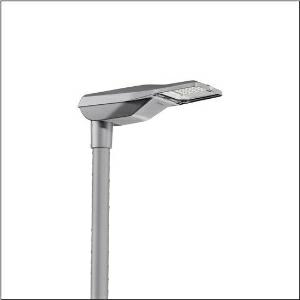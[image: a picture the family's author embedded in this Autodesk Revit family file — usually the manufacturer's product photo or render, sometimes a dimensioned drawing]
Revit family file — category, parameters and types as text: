
# Revit family: streetlight_sl_21_iq_micro___st0_8a_5xe1c31d08cb_88cc
name_source: partatom
category: Lighting Fixtures
units: mm (PartAtom-declared; Revit-internal decimal feet)

## family parameters
Cut with Voids When Loaded = No
Host = Face
Light Source = No
Part Type = Normal
Room Calculation Point = No
Round Connector Dimension = Use Diameter
Shared = No

## types (1)
- --- (1 x LED, 2870 lm, 19.4 W, 3000K)
    Apparent Load = 19 VA
    CIE Flux Codes = 38 75 97 100 100
    Color Rendering = 70
    Color Temperature = 3000K
    Default Elevation = 1800 mm
    Description = Streetlight SL 21 iQ micro, mast luminaire, primary light control with lens, of PMMA, primary optical cover: cover, of toughened safety glass, transparent, light distribution: ST0.8a, light emission: direct distribution, primary light characteristic: asymmetric, installation type: post-top, side-entry, LED, High Power LED, rated luminous flux: 2.870lm, luminous efficacy: 148lm/W, light colour: 730, colour temperature: 3000K, control gear: iQ-Comfort, control: Auto-Match, Temp-Guard, Lumen-Switch, Night-Set, Smart-Wire, Light-Fading, Desk-Remote (wireless, voltage-free reading and setting of iQ features in the workshop via application-optimized NFC function/RFID function), optimised constant luminous flux control (CLO 2.0), pre-setting: linear dimming characteristic, mains connection: 220..240V, AC, 50/60Hz, start of lifetime: 19W, end of service life: 20W, reduction: 10W, luminaire housing, of diecast aluminium, powder-coated, Siteco® metallic grey (DB 702S), corrosivity category C5 mid according to DIN EN ISO 12944, please order mast flange separately, inclination adjustable: 0°, 5°, 10°, 15°, sealing non-destructively replaceable, multi-level sealing system, length: 528mm, width: 235mm, height: 110mm, mast flange for spigot size: 42mm (side-entry): 5XC10008XM4, 60/48mm (side-entry/post-top): 5XC10108XM2, 76/60mm (side-entry/post-top): 5XC10108XM1, protection rating (complete): IP66, insulation class (complete): insulation class II (safety insulation), certification: CE, ENEC, ENEC+, VDE, impact resistance: IK10, permissible operating ambient temperature for outdoor applications: -40..+50°C, standard-compliant lighting for roads and squares, packaging unit: 1 piece

Light Distribution: ST0.8a
    Height = 110 mm
    Lamp = 1 x LED
    Lamp Light Flux = 2870 lm
    Lamp Power = 19.4 W
    Lamp count = 1
    Length = 528 mm
    Luminous efficacy = 148 lm/W
    Manufacturer = Siteco
    ModVariant = No
    Model = 5XE1C31D08CB
    Number of Poles = 1
    OnlyDefault = Yes
    Power Factor = 1
    Product Name = Streetlight SL 21 iQ micro | ST0.8a
    Product group = mast luminaire | pylon top
    ProductGroupID = 6100
    Protection Class = Protection class II
    Protection Degree = IP 66
    RLX_Detail_Level = 1
    RLX_Emergency_Light_Flux = 0 lm
    RLX_Emergency_Type = 0
    RLX_Emergency_Type_DB = No
    RlxData = <blob elided: 98749 chars, md5=b8607aac>
    Socket = socket
    Standby Power = 0 W
    System Light Flux = 2870 lm
    System Power = 19 W
    Type Comments = factory setting: luminous flux: 100 % | dim-lin: 254 | 387 mA
    Type Image = l_1006881.jpg
    URL = http://relux.com
    VarID = @adj_159943
    Voltage = 0 V
    Weight = 0.00 kg
    Width = 235 mm

## geometry (parser evidence)
native form markers: Blend x4, Sweep x12
no freeform markers — native parametric forms only
